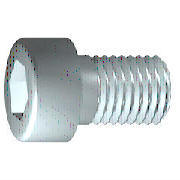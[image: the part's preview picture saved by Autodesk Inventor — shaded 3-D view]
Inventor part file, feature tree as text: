
AUTODESK INVENTOR PART (.ipt)
format: ipt  version: 2021 (Build 250183000, 183)  size: 198,656 bytes
history: native  units: mm (DEFAULTED — no unit token found)
features: sketch x2, extrude x1, plane x1, fillet x1
ambient origin geometry x7: Origin, YZ Plane, XY Plane, X Axis, Y Axis, Z Axis, Center Point
bodies: Solid1 (feature_tree), Body (feature_tree)
feature tree (5):
  extrude  "Slot"  Depth=12.0mm
  plane  "Work Plane1"
  fillet  "Fillet2"  Radius=12.0mm
  sketch  "Sketch1"  dims[d1=15.625mm d2=1.073638mm d3=12.0mm]
  sketch  "Sketch2"  dims[d4=6.0mm d5=60.0deg d6=12.0mm d7=12.0mm d8=11.547005mm d9=18.0mm d10=90.0deg d11=10.0mm d12=0.0mm d13=15.625mm d14=0.0mm d15=1.073538mm d16=1.073538mm d17=1.2mm d19=0.0mm d26=20.0mm d27=45.0deg d28=0.0mm d29=0.0mm d30=0.1mm]
